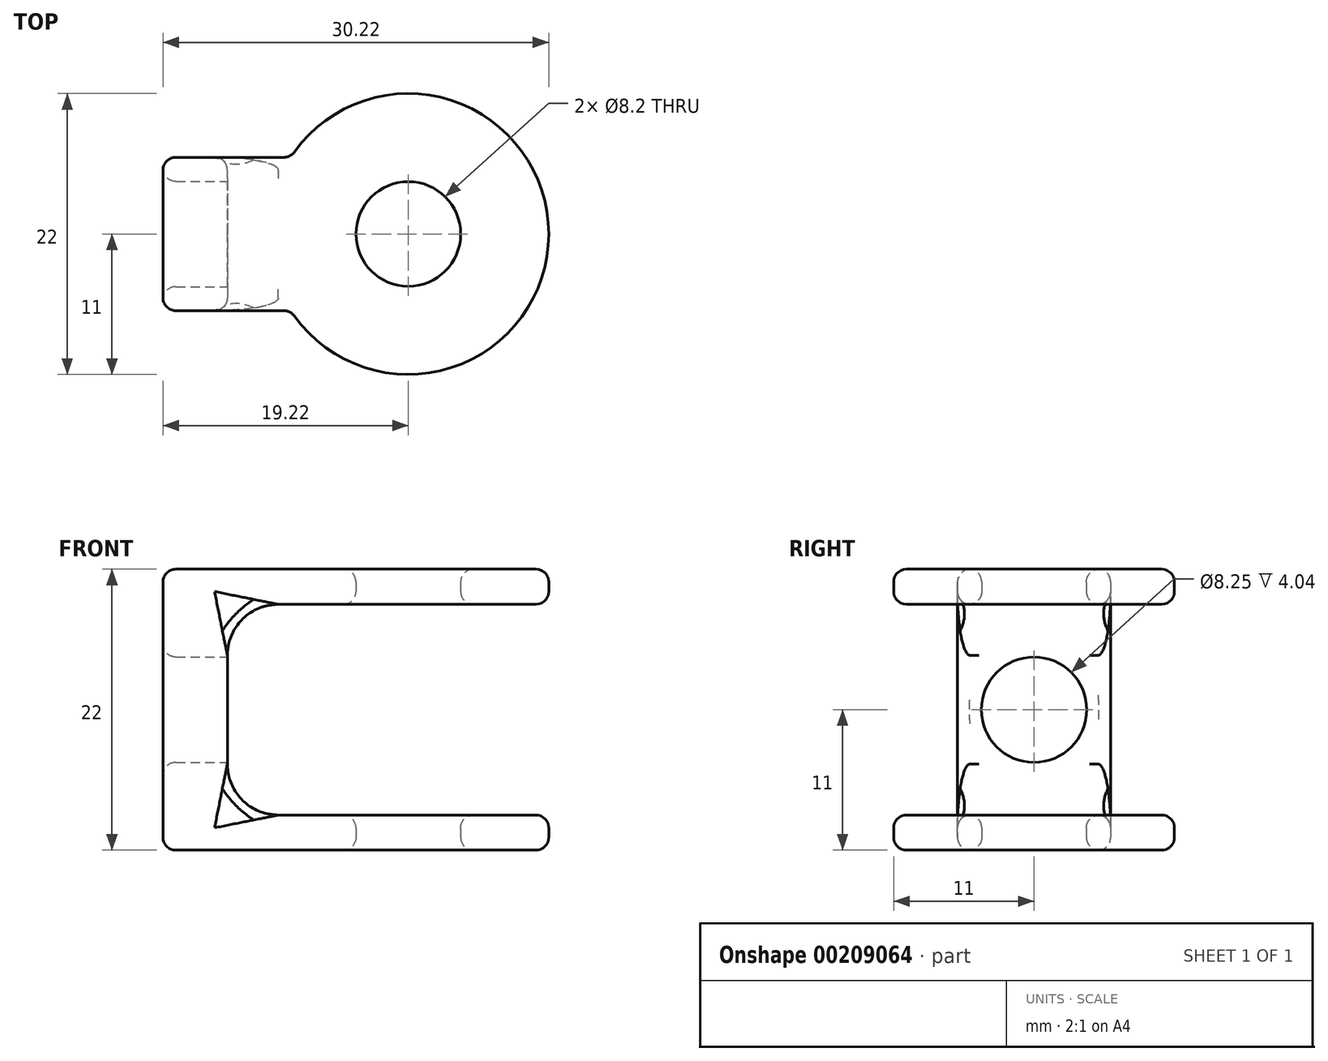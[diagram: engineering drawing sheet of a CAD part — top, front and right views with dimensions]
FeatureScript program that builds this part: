
annotation { "Feature Type Name" : "Feature", "Feature Type Description" : "" }
export const myFeature = defineFeature(function(context is Context, id is Id, definition is map)
    precondition{}
    {
        {
            var Q0;
            Q0=qCreatedBy(makeId("Top.planeOp"),FACE);
            var sketch = newSketch(context, id + "F0", { "sketchPlane" : qUnion([Q0])});
            skLineSegment(sketch, "E0.bottom", {"start": v(-19.22, 6) * mm, "end": v(-9.22, 6) * mm});
            skLineSegment(sketch, "E0.top", {"start": v(-19.22, -6) * mm, "end": v(-9.22, -6) * mm});
            skLineSegment(sketch, "E0.left", {"start": v(-19.22, 6) * mm, "end": v(-19.22, -6) * mm});
            skArc(sketch, "E1", {"start": v(-9.22, 6) * mm, "mid": v(11, 0) * mm, "end": v(-9.22, -6) * mm});
            skLineSegment(sketch, "E2", {"start": v(-9.22, 6) * mm, "end": v(-9.22, -6) * mm, "construction": true});
            skCircle(sketch, "E3", {"center": v(0, 0) * mm, "radius": 4.1 * mm});
            skSolve(sketch);
        }
        {
            var Q0;
            Q0=qSketchRegion(id+"F0",true);
            extrude(context, id + "F1", {"entities" : qUnion([Q0]), "depth" : 22 * mm});
        }
        {
            var Q0;
            Q0=makeQuery(id+"F1.opExtrude","SWEPT_FACE",FACE,{"disambiguationData":[OSD([sQuery(id+"F0.wireOp",EDGE,"E0.top")])]});
            var sketch = newSketch(context, id + "F2", { "sketchPlane" : qUnion([Q0])});
            skLineSegment(sketch, "E4.bottom", {"start": v(-14.18, 19.25) * mm, "end": v(11.04, 19.25) * mm});
            skLineSegment(sketch, "E4.top", {"start": v(-14.18, 2.75) * mm, "end": v(11.04, 2.75) * mm});
            skLineSegment(sketch, "E4.left", {"start": v(-14.18, 19.25) * mm, "end": v(-14.18, 2.75) * mm});
            skLineSegment(sketch, "E4.right", {"start": v(11.04, 19.25) * mm, "end": v(11.04, 2.75) * mm});
            skLineSegment(sketch, "E5", {"start": v(-14.18, 2.75) * mm, "end": v(-14.18, 0) * mm, "construction": true});
            skLineSegment(sketch, "E6", {"start": v(-14.18, 19.25) * mm, "end": v(-14.18, 22) * mm, "construction": true});
            skSolve(sketch);
        }
        {
            var Q0;
            Q0=qSketchRegion(id+"F2",true);
            extrude(context, id + "F3", {"entities" : qUnion([Q0]), "operationType" : NewBodyOperationType.REMOVE, "endBound" : BoundingType.THROUGH_ALL, "oppositeDirection" : true, "depth" : 25 * mm, "hasSecondDirection" : true, "secondDirectionBound" : SecondDirectionBoundingType.THROUGH_ALL, "secondDirectionOppositeDirection" : false, "secondDirectionDepth" : 25 * mm});
        }
        {
            var Q0;
            Q0=makeQuery(id+"F3.boolean.opBoolean","COPY",FACE,{"derivedFrom":makeQuery(id+"F3.opExtrude","SWEPT_FACE",FACE,{"disambiguationData":[OSD([sQuery(id+"F2.wireOp",EDGE,"E4.left")])]})});
            var sketch = newSketch(context, id + "F4", { "sketchPlane" : qUnion([Q0])});
            skCircle(sketch, "E7", {"center": v(0, 11) * mm, "radius": 4.12 * mm});
            skLineSegment(sketch, "E8", {"start": v(0, 11) * mm, "end": v(0, 19.25) * mm, "construction": true});
            skLineSegment(sketch, "E9", {"start": v(0, 11) * mm, "end": v(0, 2.75) * mm, "construction": true});
            skSolve(sketch);
        }
        {
            var Q0;
            Q0=qSketchRegion(id+"F4",true);
            extrude(context, id + "F5", {"entities" : qUnion([Q0]), "operationType" : NewBodyOperationType.REMOVE, "endBound" : BoundingType.THROUGH_ALL, "oppositeDirection" : true, "depth" : 25 * mm});
        }
        {
            var Q0;
            Q0=makeQuery(id+"F1.opExtrude","SWEPT_FACE",FACE,{"disambiguationData":[OSD([sQuery(id+"F0.wireOp",EDGE,"E0.left")])]});
            var Q1;
            Q1=makeQuery(id+"F5.boolean.opBoolean","INTERSECT",EDGE,{"derivedFrom":[makeQuery(id+"F1.opExtrude","SWEPT_FACE",FACE,{"disambiguationData":[OSD([sQuery(id+"F0.wireOp",EDGE,"E0.left")])]}),makeQuery(id+"F5.opExtrude","SWEPT_FACE",FACE,{"disambiguationData":[OSD([sQuery(id+"F4.wireOp",EDGE,"E7")])]})]});
            fillet(context, id + "F6", {"entities" : qUnion([Q0, Q1]), "radius" : 1 * mm, "tangentPropagation" : true, "allowEdgeOverflow" : false});
        }
        {
            var Q0;
            Q0=makeQuery(id+"F1.opExtrude","CAP_EDGE",EDGE,{"disambiguationData":[OSD([sQuery(id+"F0.wireOp",EDGE,"E3")])],"isStart":true});
            var Q1;
            Q1=makeQuery(id+"F3.boolean.opBoolean","INTERSECT",EDGE,{"derivedFrom":[makeQuery(id+"F1.opExtrude","SWEPT_FACE",FACE,{"disambiguationData":[OSD([sQuery(id+"F0.wireOp",EDGE,"E3")])]}),makeQuery(id+"F3.opExtrude","SWEPT_FACE",FACE,{"disambiguationData":[OSD([sQuery(id+"F2.wireOp",EDGE,"E4.top")])]})]});
            var Q2;
            Q2=makeQuery(id+"F3.boolean.opBoolean","INTERSECT",EDGE,{"derivedFrom":[makeQuery(id+"F1.opExtrude","SWEPT_FACE",FACE,{"disambiguationData":[OSD([sQuery(id+"F0.wireOp",EDGE,"E3")])]}),makeQuery(id+"F3.opExtrude","SWEPT_FACE",FACE,{"disambiguationData":[OSD([sQuery(id+"F2.wireOp",EDGE,"E4.bottom")])]})]});
            var Q3;
            Q3=makeQuery(id+"F1.opExtrude","CAP_EDGE",EDGE,{"disambiguationData":[OSD([sQuery(id+"F0.wireOp",EDGE,"E3")])],"isStart":false});
            fillet(context, id + "F7", {"entities" : qUnion([Q0, Q1, Q2, Q3]), "radius" : 1 * mm, "tangentPropagation" : true, "allowEdgeOverflow" : false});
        }
        {
            var Q0;
            {var subQ1=sQuery(id+"F0.wireOp",EDGE,"E1");Q0=makeQuery(id+"F3.boolean.opBoolean","SPLIT",FACE,{"disambiguationData":[TD([makeQuery(id+"F3.opExtrude","SWEPT_FACE",FACE,{"disambiguationData":[OSD([sQuery(id+"F2.wireOp",EDGE,"E4.bottom")])]})])],"derivedFrom":makeQuery(id+"F1.opExtrude","SWEPT_FACE",FACE,{"disambiguationData":[OSD([subQ1])]})});}
            var Q1;
            {var subQ1=sQuery(id+"F0.wireOp",EDGE,"E1");Q1=makeQuery(id+"F3.boolean.opBoolean","SPLIT",FACE,{"disambiguationData":[TD([makeQuery(id+"F3.opExtrude","SWEPT_FACE",FACE,{"disambiguationData":[OSD([sQuery(id+"F2.wireOp",EDGE,"E4.top")])]})])],"derivedFrom":makeQuery(id+"F1.opExtrude","SWEPT_FACE",FACE,{"disambiguationData":[OSD([subQ1])]})});}
            var Q2;
            Q2=makeQuery(id+"F1.opExtrude","SWEPT_FACE",FACE,{"disambiguationData":[OSD([sQuery(id+"F0.wireOp",EDGE,"E0.top")])]});
            var Q3;
            Q3=makeQuery(id+"F1.opExtrude","SWEPT_FACE",FACE,{"disambiguationData":[OSD([sQuery(id+"F0.wireOp",EDGE,"E0.bottom")])]});
            fillet(context, id + "F8", {"entities" : qUnion([Q0, Q1, Q2, Q3]), "radius" : 1 * mm, "tangentPropagation" : true, "allowEdgeOverflow" : false});
        }
        {
            var Q0;
            Q0=makeQuery(id+"F3.boolean.opBoolean","COPY",EDGE,{"derivedFrom":makeQuery(id+"F3.opExtrude","SWEPT_EDGE",EDGE,{"disambiguationData":[OSD([sQuery(id+"F2.wireOp",EDGE,"E4.bottom"),sQuery(id+"F2.wireOp",EDGE,"E4.left")])]})});
            var Q1;
            Q1=makeQuery(id+"F3.boolean.opBoolean","COPY",EDGE,{"derivedFrom":makeQuery(id+"F3.opExtrude","SWEPT_EDGE",EDGE,{"disambiguationData":[OSD([sQuery(id+"F2.wireOp",EDGE,"E4.top"),sQuery(id+"F2.wireOp",EDGE,"E4.left")])]})});
            fillet(context, id + "F9", {"entities" : qUnion([Q0, Q1]), "radius" : 4 * mm, "tangentPropagation" : true, "allowEdgeOverflow" : false});
        }
    });
